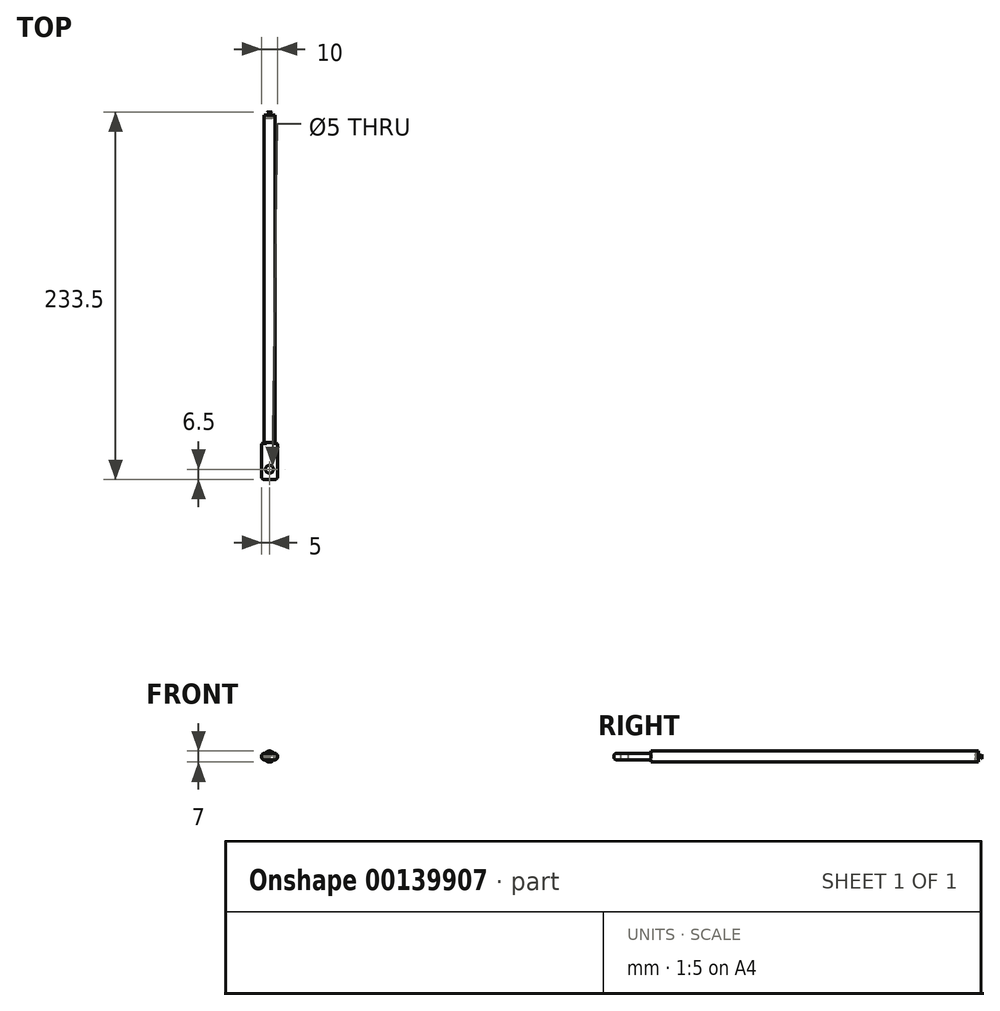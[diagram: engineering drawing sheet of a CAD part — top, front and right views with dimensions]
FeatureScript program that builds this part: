
annotation { "Feature Type Name" : "Feature", "Feature Type Description" : "" }
export const myFeature = defineFeature(function(context is Context, id is Id, definition is map)
    precondition{}
    {
        {
            var Q0;
            Q0=qCreatedBy(makeId("Top.planeOp"),FACE);
            var sketch = newSketch(context, id + "F0", { "sketchPlane" : qUnion([Q0])});
            skCircle(sketch, "E0", {"center": v(0, 0) * mm, "radius": 2.5 * mm});
            skLineSegment(sketch, "E1", {"start": v(0, 0) * mm, "end": v(0, -6.5) * mm, "construction": true});
            skLineSegment(sketch, "E2", {"start": v(-5, -6.5) * mm, "end": v(5, -6.5) * mm});
            skLineSegment(sketch, "E3", {"start": v(0, 0) * mm, "end": v(0, 17) * mm, "construction": true});
            skLineSegment(sketch, "E4", {"start": v(-3.5, 17) * mm, "end": v(3.5, 17) * mm});
            skPoint(sketch, "E5", {"position": v(0, 5.25) * mm});
            skLineSegment(sketch, "E6", {"start": v(5, -6.5) * mm, "end": v(5, 8.5) * mm});
            skPoint(sketch, "E7.visualSharp", {"position": v(5, 17) * mm});
            skLineSegment(sketch, "E8", {"start": v(5, 8.5) * mm, "end": v(5, 15.5) * mm});
            skArc(sketch, "E9", {"start": v(5, 15.5) * mm, "mid": v(4.56, 16.56) * mm, "end": v(3.5, 17) * mm});
            skLineSegment(sketch, "E10", {"start": v(-5, -6.5) * mm, "end": v(-5, 15.5) * mm});
            skArc(sketch, "E11", {"start": v(-3.5, 17) * mm, "mid": v(-4.56, 16.56) * mm, "end": v(-5, 15.5) * mm});
            skSolve(sketch);
        }
        {
            var Q0;
            Q0=qCreatedBy(makeId("Front.planeOp"),FACE);
            cPlane(context, id + "F1", {"entities" : qUnion([Q0]), "cplaneType" : CPlaneType.OFFSET, "offset" : 17 * mm, "oppositeDirection" : true, "width" : 150 * mm, "height" : 150 * mm});
        }
        {
            var Q0;
            Q0=qCreatedBy(id+"F1.planeOp",FACE);
            var sketch = newSketch(context, id + "F2", { "sketchPlane" : qUnion([Q0])});
            skPoint(sketch, "E12.0", {"position": v(0, 0) * mm});
            skCircle(sketch, "E13", {"center": v(0, 0) * mm, "radius": 3.5 * mm});
            skSolve(sketch);
        }
        {
            var Q0;
            Q0 = qSketchRegion(id + "F2", true);
            extrude(context, id + "F3", {"entities" : qUnion([Q0]), "oppositeDirection" : true, "depth" : 210 * mm});
        }
        {
            var Q0;
            Q0 = qSketchRegion(id + "F0", true);
            extrude(context, id + "F4", {"entities" : qUnion([Q0]), "operationType" : NewBodyOperationType.ADD, "endBound" : BoundingType.SYMMETRIC, "depth" : 4 * mm});
        }
        {
            var Q0;
            Q0=makeQuery(id+"F4.opExtrude","SWEPT_EDGE",EDGE,{"disambiguationData":[OSD([sQuery(id+"F0.wireOp",EDGE,"E2"),sQuery(id+"F0.wireOp",EDGE,"E6")])]});
            fillet(context, id + "F5", {"entities" : qUnion([Q0]), "radius" : 1.5 * mm, "tangentPropagation" : true, "allowEdgeOverflow" : false});
        }
        {
            var Q0;
            Q0=makeQuery(id+"F4.opExtrude","SWEPT_EDGE",EDGE,{"disambiguationData":[OSD([sQuery(id+"F0.wireOp",EDGE,"E2"),sQuery(id+"F0.wireOp",EDGE,"E10")])]});
            fillet(context, id + "F6", {"entities" : qUnion([Q0]), "radius" : 1.5 * mm, "tangentPropagation" : true, "allowEdgeOverflow" : false});
        }
        {
            var Q0;
            {var subQ0=sQuery(id+"F2.wireOp",EDGE,"E13");var subQ1=sQuery(id+"F0.wireOp",EDGE,"E4");Q0=makeQuery(id+"F4.boolean.opBoolean","SPLIT",EDGE,{"disambiguationData":[TD([makeQuery(id+"F3.opExtrude","SWEPT_FACE",FACE,{"disambiguationData":[OSD([subQ0])]}),makeQuery(id+"F3.opExtrude","CAP_FACE",FACE,{"disambiguationData":[OSD([subQ0])],"isStart":true}),makeQuery(id+"F4.opExtrude","CAP_FACE",FACE,{"disambiguationData":[OSD([sQuery(id+"F0.wireOp",EDGE,"E0"),sQuery(id+"F0.wireOp",EDGE,"E2"),subQ1,sQuery(id+"F0.wireOp",EDGE,"E6"),sQuery(id+"F0.wireOp",EDGE,"E8"),sQuery(id+"F0.wireOp",EDGE,"E9"),sQuery(id+"F0.wireOp",EDGE,"E10"),sQuery(id+"F0.wireOp",EDGE,"E11")])],"isStart":false}),makeQuery(id+"F4.opExtrude","SWEPT_FACE",FACE,{"disambiguationData":[OSD([subQ1])]})])],"derivedFrom":makeQuery(id+"F4.opExtrude","CAP_EDGE",EDGE,{"disambiguationData":[OSD([subQ1])],"isStart":false})});}
            fillet(context, id + "F7", {"entities" : qUnion([Q0]), "radius" : 1.5 * mm, "tangentPropagation" : true, "allowEdgeOverflow" : false});
        }
        {
            var Q0;
            {var subQ0=sQuery(id+"F2.wireOp",EDGE,"E13");var subQ1=sQuery(id+"F0.wireOp",EDGE,"E4");Q0=makeQuery(id+"F4.boolean.opBoolean","SPLIT",EDGE,{"disambiguationData":[TD([makeQuery(id+"F3.opExtrude","SWEPT_FACE",FACE,{"disambiguationData":[OSD([subQ0])]}),makeQuery(id+"F3.opExtrude","CAP_FACE",FACE,{"disambiguationData":[OSD([subQ0])],"isStart":true}),makeQuery(id+"F4.opExtrude","CAP_FACE",FACE,{"disambiguationData":[OSD([sQuery(id+"F0.wireOp",EDGE,"E0"),sQuery(id+"F0.wireOp",EDGE,"E2"),subQ1,sQuery(id+"F0.wireOp",EDGE,"E6"),sQuery(id+"F0.wireOp",EDGE,"E8"),sQuery(id+"F0.wireOp",EDGE,"E9"),sQuery(id+"F0.wireOp",EDGE,"E10"),sQuery(id+"F0.wireOp",EDGE,"E11")])],"isStart":true}),makeQuery(id+"F4.opExtrude","SWEPT_FACE",FACE,{"disambiguationData":[OSD([subQ1])]})])],"derivedFrom":makeQuery(id+"F4.opExtrude","CAP_EDGE",EDGE,{"disambiguationData":[OSD([subQ1])],"isStart":true})});}
            fillet(context, id + "F8", {"entities" : qUnion([Q0]), "radius" : 1.5 * mm, "tangentPropagation" : true, "allowEdgeOverflow" : false});
        }
        {
            var Q0;
            Q0=makeQuery(id+"F3.opExtrude","CAP_EDGE",EDGE,{"disambiguationData":[OSD([sQuery(id+"F2.wireOp",EDGE,"E13")])],"isStart":false});
            fillet(context, id + "F9", {"entities" : qUnion([Q0]), "radius" : 2 * mm, "tangentPropagation" : true, "allowEdgeOverflow" : false});
        }
    });
